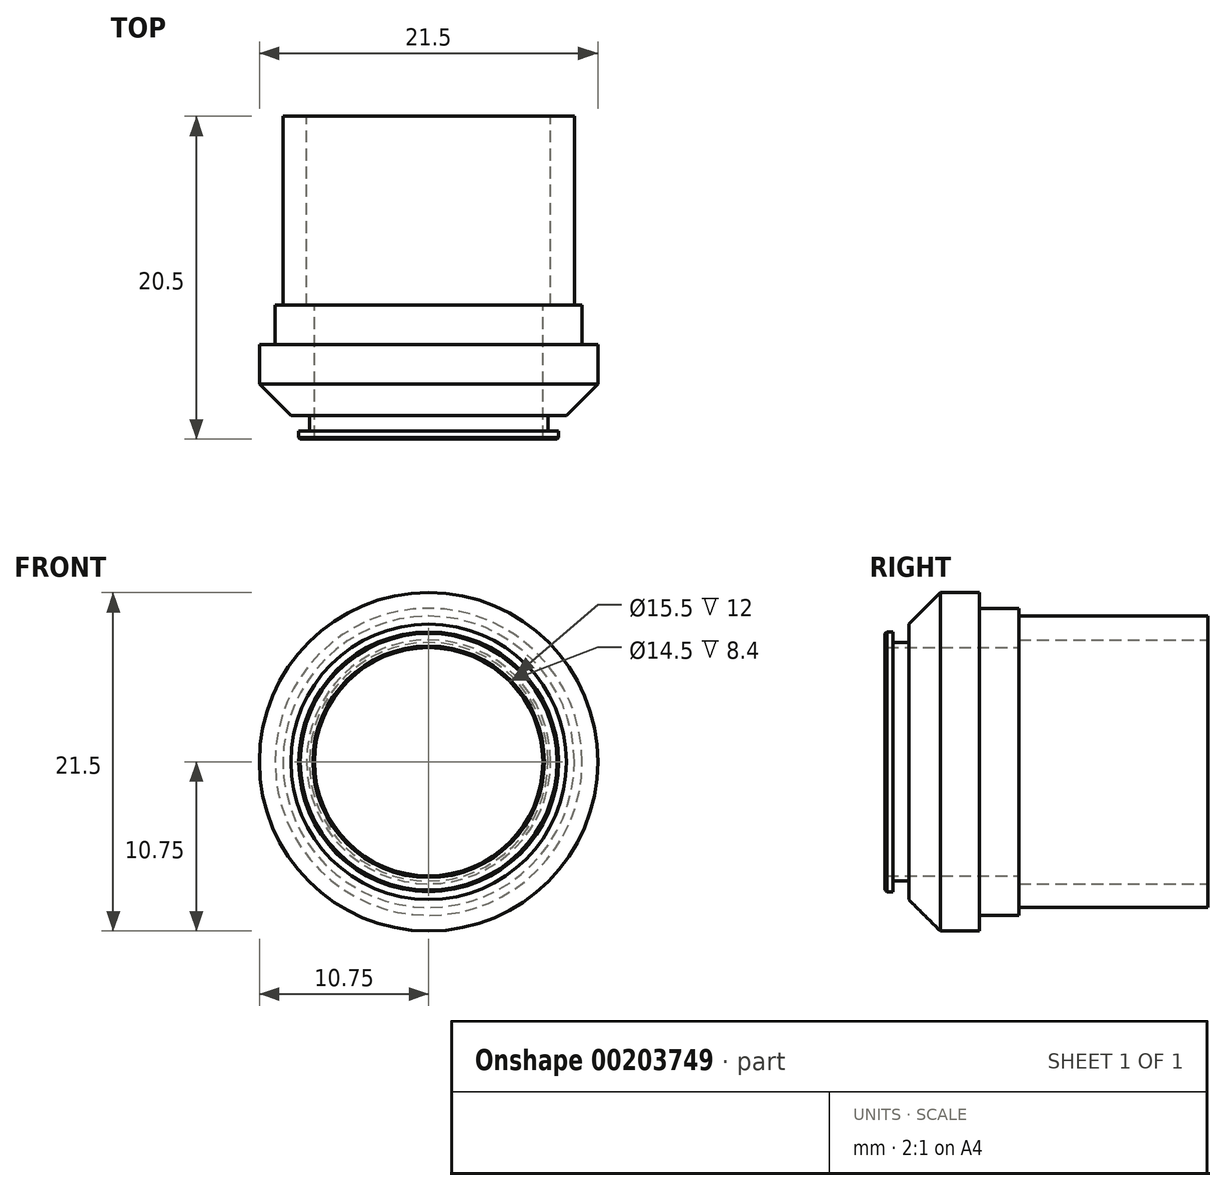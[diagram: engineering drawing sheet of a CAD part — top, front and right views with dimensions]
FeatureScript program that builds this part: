
annotation { "Feature Type Name" : "Feature", "Feature Type Description" : "" }
export const myFeature = defineFeature(function(context is Context, id is Id, definition is map)
    precondition{}
    {
        {
            var Q0;
            Q0=qCreatedBy(makeId("Front.planeOp"),FACE);
            var sketch = newSketch(context, id + "F0", { "sketchPlane" : qUnion([Q0])});
            skCircle(sketch, "E0", {"center": v(0, 0) * mm, "radius": 9.25 * mm});
            skCircle(sketch, "E1", {"center": v(0, 0) * mm, "radius": 7.75 * mm});
            skSolve(sketch);
        }
        {
            var Q0;
            Q0 = qSketchRegion(id + "F0", true);
            extrude(context, id + "F1", {"entities" : qUnion([Q0]), "depth" : 12 * mm});
        }
        {
            var Q0;
            Q0=makeQuery(id+"F1.opExtrude","CAP_FACE",FACE,{"disambiguationData":[OSD([sQuery(id+"F0.wireOp",EDGE,"E0"),sQuery(id+"F0.wireOp",EDGE,"E1")])],"isStart":false});
            var sketch = newSketch(context, id + "F2", { "sketchPlane" : qUnion([Q0])});
            skCircle(sketch, "E2", {"center": v(0, 0) * mm, "radius": 7.25 * mm});
            skCircle(sketch, "E3", {"center": v(0, 0) * mm, "radius": 9.75 * mm});
            skSolve(sketch);
        }
        {
            var Q0;
            Q0 = qSketchRegion(id + "F2", true);
            extrude(context, id + "F3", {"entities" : qUnion([Q0]), "operationType" : NewBodyOperationType.ADD, "depth" : 2.5 * mm});
        }
        {
            var Q0;
            Q0=makeQuery(id+"F3.opExtrude","CAP_FACE",FACE,{"disambiguationData":[OSD([sQuery(id+"F2.wireOp",EDGE,"E2"),sQuery(id+"F2.wireOp",EDGE,"E3")])],"isStart":false});
            var sketch = newSketch(context, id + "F4", { "sketchPlane" : qUnion([Q0])});
            skCircle(sketch, "E4", {"center": v(0, 0) * mm, "radius": 7.25 * mm});
            skCircle(sketch, "E5", {"center": v(0, 0) * mm, "radius": 10.75 * mm});
            skSolve(sketch);
        }
        {
            var Q0;
            Q0 = qSketchRegion(id + "F4", true);
            extrude(context, id + "F5", {"entities" : qUnion([Q0]), "operationType" : NewBodyOperationType.ADD, "depth" : 4.5 * mm});
        }
        {
            var Q0;
            Q0=makeQuery(id+"F5.opExtrude","CAP_EDGE",EDGE,{"disambiguationData":[OSD([sQuery(id+"F4.wireOp",EDGE,"E5")])],"isStart":false});
            chamfer(context, id + "F6", {"entities" : qUnion([Q0]), "width" : 2 * mm, "tangentPropagation" : true});
        }
        {
            var Q0;
            Q0=makeQuery(id+"F5.opExtrude","CAP_FACE",FACE,{"disambiguationData":[OSD([sQuery(id+"F4.wireOp",EDGE,"E4"),sQuery(id+"F4.wireOp",EDGE,"E5")])],"isStart":false});
            var sketch = newSketch(context, id + "F7", { "sketchPlane" : qUnion([Q0])});
            skCircle(sketch, "E6", {"center": v(0, 0) * mm, "radius": 7.25 * mm});
            skCircle(sketch, "E7", {"center": v(0, 0) * mm, "radius": 7.58 * mm});
            skSolve(sketch);
        }
        {
            var Q0;
            Q0 = qSketchRegion(id + "F7", true);
            extrude(context, id + "F8", {"entities" : qUnion([Q0]), "operationType" : NewBodyOperationType.ADD, "depth" : 1 * mm});
        }
        {
            var Q0;
            Q0=makeQuery(id+"F8.opExtrude","CAP_FACE",FACE,{"disambiguationData":[OSD([sQuery(id+"F7.wireOp",EDGE,"E6"),sQuery(id+"F7.wireOp",EDGE,"E7")])],"isStart":false});
            var sketch = newSketch(context, id + "F9", { "sketchPlane" : qUnion([Q0])});
            skCircle(sketch, "E8", {"center": v(0, 0) * mm, "radius": 7.25 * mm});
            skCircle(sketch, "E9", {"center": v(0, 0) * mm, "radius": 8.25 * mm});
            skSolve(sketch);
        }
        {
            var Q0;
            Q0=makeQuery(id+"F9.imprint","IMPRINT",FACE,{"disambiguationData":[TD([[makeQuery(id+"F9.imprint","IMPRINT",EDGE,{"derivedFrom":sQuery(id+"F9.wireOp",EDGE,"E8")}),-1.0]])]});
            var Q1;
            Q1=makeQuery(id+"F9.imprint","IMPRINT",FACE,{"disambiguationData":[TD([[makeQuery(id+"F9.imprint","IMPRINT",EDGE,{"derivedFrom":sQuery(id+"F9.wireOp",EDGE,"E9")}),1.0]])]});
            extrude(context, id + "F10", {"entities" : qUnion([Q0, Q1]), "operationType" : NewBodyOperationType.ADD, "depth" : 0.5 * mm});
        }
        {
            var Q0;
            Q0=makeQuery(id+"F10.opExtrude","CAP_FACE",FACE,{"disambiguationData":[OSD([sQuery(id+"F9.wireOp",EDGE,"E8"),sQuery(id+"F9.wireOp",EDGE,"E9")])],"isStart":false});
            chamfer(context, id + "F11", {"entities" : qUnion([Q0]), "width" : 0.1 * mm, "tangentPropagation" : true});
        }
    });
